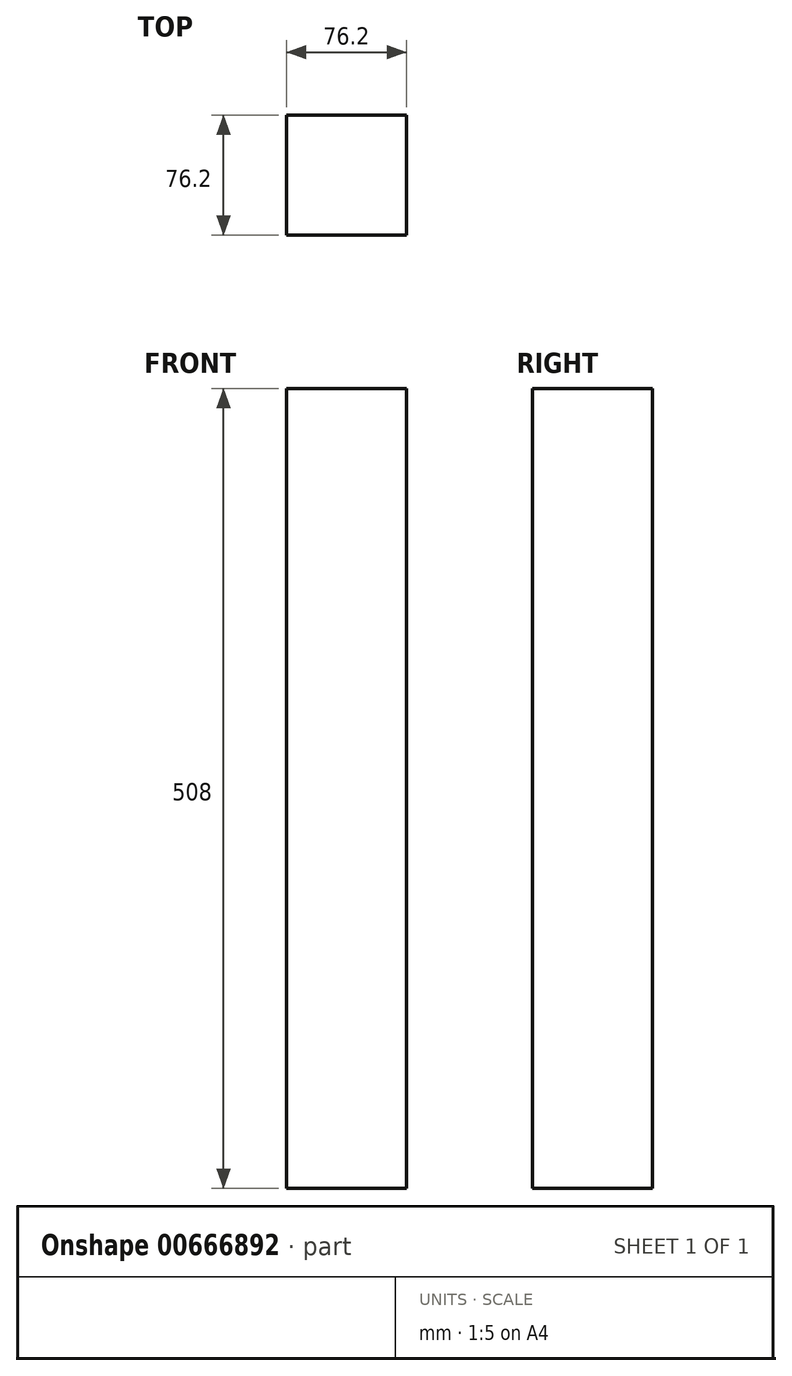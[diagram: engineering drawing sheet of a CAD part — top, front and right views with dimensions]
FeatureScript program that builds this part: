
annotation { "Feature Type Name" : "Feature", "Feature Type Description" : "" }
export const myFeature = defineFeature(function(context is Context, id is Id, definition is map)
    precondition{}
    {
        {
            var Q0;
            Q0=qCreatedBy(makeId("Top.planeOp"),FACE);
            var sketch = newSketch(context, id + "F0", { "sketchPlane" : qUnion([Q0])});
            skLineSegment(sketch, "E0.bottom", {"start": v(0, 0) * mm, "end": v(76.2, 0) * mm});
            skLineSegment(sketch, "E0.top", {"start": v(0, -76.2) * mm, "end": v(76.2, -76.2) * mm});
            skLineSegment(sketch, "E0.left", {"start": v(0, 0) * mm, "end": v(0, -76.2) * mm});
            skLineSegment(sketch, "E0.right", {"start": v(76.2, 0) * mm, "end": v(76.2, -76.2) * mm});
            skSolve(sketch);
        }
        {
            var Q0;
            Q0=makeQuery(id+"F0.imprint","IMPRINT",FACE,{"disambiguationData":[TD([[makeQuery(id+"F0.imprint","IMPRINT",EDGE,{"derivedFrom":sQuery(id+"F0.wireOp",EDGE,"E0.bottom")}),-1.0]])]});
            extrude(context, id + "F1", {"entities" : qUnion([Q0]), "depth" : 508 * mm, "offsetDistance" : 25.4 * mm});
        }
    });
